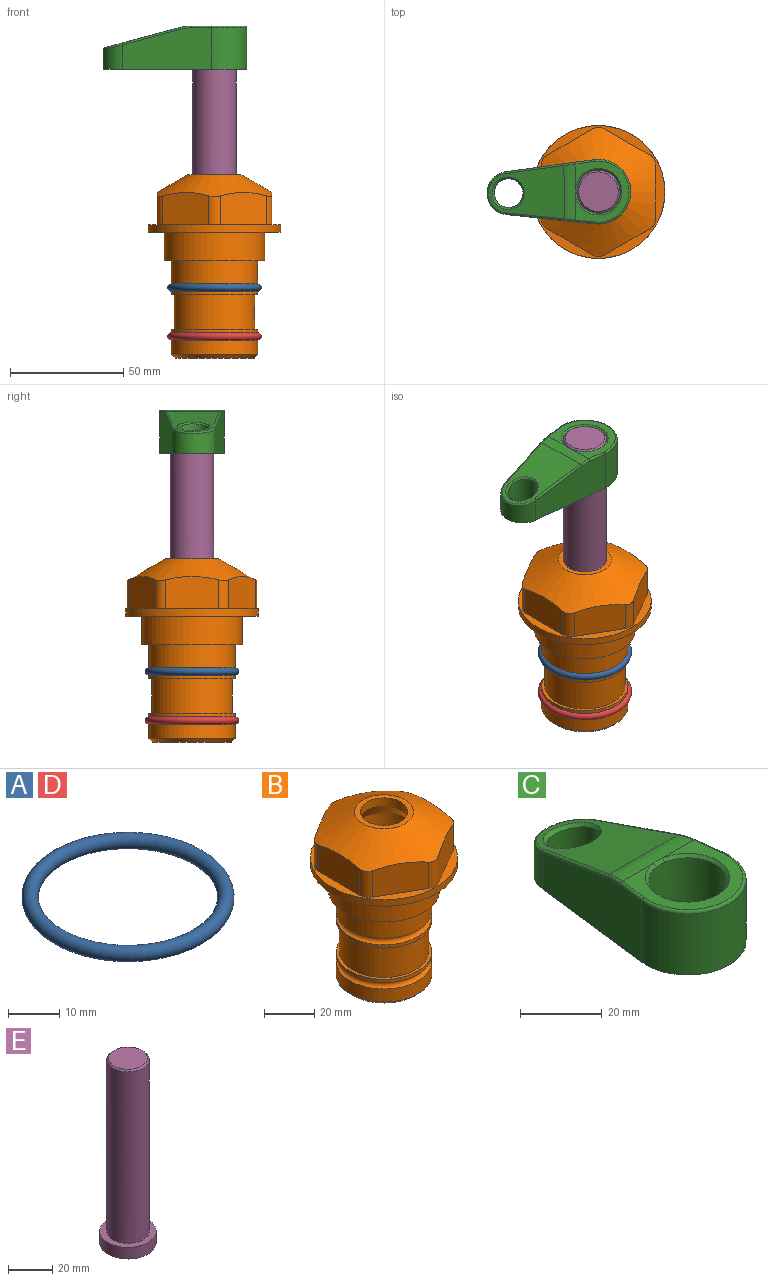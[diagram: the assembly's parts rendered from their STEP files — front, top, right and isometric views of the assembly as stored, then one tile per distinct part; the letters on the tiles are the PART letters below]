
ASSEMBLY  parts=5 mates=3
PART A: 1 faces, bbox 44.7x44.7x3.2 mm
  f0: torus R=19.05mm, axis (0,0,1), area 1193.9mm2
PART B: 36 faces, bbox 58.7x58.7x81 mm
  f0: cylinder r=17.78mm len=35.56mm, axis (0,0,1), area 1670.8mm2, adj f23,f24,f31
  f1: cylinder r=19.05mm len=38.1mm, axis (0,0,1), area 1191.9mm2, adj f26,f27,f30
  f2: plane 58.66x58.66mm, normal (0,0,-1), area 1150.6mm2, adj f3,f28
  f3: cylinder r=29.33mm len=58.66mm, axis (0,0,-1), area 585.1mm2, adj f2,f4
  f4: plane 58.66x58.66mm, normal (0,0,1), area 475.9mm2, adj f3,f5,f6,f7,f8,f9,f10,f11
  f5: plane 20.32x14.34mm, normal (-0.5,0.87,0), area 324.4mm2, adj f4,f15,f16,f17
  f6: plane 20.32x14.34mm, normal (0.5,0.87,0), area 324.4mm2, adj f4,f14,f15,f17
  f7: plane 23.48x14.34mm, normal (1,0,0), area 324.4mm2, adj f4,f13,f14,f17
  f8: plane 20.32x14.34mm, normal (0.5,-0.87,0), area 324.4mm2, adj f4,f12,f13,f17
  f9: plane 20.32x14.34mm, normal (-0.5,-0.87,0), area 324.4mm2, adj f4,f11,f12,f17
  f10: plane 23.48x14.34mm, normal (-1,0,0), area 324.4mm2, adj f4,f11,f16,f17
  f11: cylinder r=5.08mm len=12.85mm, axis (0,0,-1), area 67.2mm2, adj f4,f9,f10,f17
  f12: cylinder r=5.08mm len=12.85mm, axis (0,0,-1), area 67.2mm2, adj f4,f8,f9,f17
  f13: cylinder r=5.08mm len=12.85mm, axis (0,0,-1), area 67.2mm2, adj f4,f7,f8,f17
  f14: cylinder r=5.08mm len=12.85mm, axis (0,0,-1), area 67.2mm2, adj f4,f6,f7,f17
  f15: cylinder r=5.08mm len=12.85mm, axis (0,0,-1), area 67.2mm2, adj f4,f5,f6,f17
  f16: cylinder r=5.08mm len=12.85mm, axis (0,0,-1), area 67.2mm2, adj f4,f5,f10,f17
  f17: cone r=11.73mm half-angle=60deg, axis (0,0,-1), area 2071.8mm2, adj f5,f6,f7,f8,f9,f10,f11,f12
  f18: plane 23.46x23.46mm, normal (0,0,1), area 147.4mm2, adj f17,f35
  f19: plane 34.93x34.93mm, normal (0,0,-1), area 958mm2, adj f29
  f20: cylinder r=19.05mm len=38.1mm, axis (0,0,1), area 760.1mm2, adj f21,f29
  f21: torus R=19.05mm, axis (0,0,1), area 565.3mm2, adj f20,f22
  f22: cylinder r=19.05mm len=38.1mm, axis (0,0,1), area 190mm2, adj f21,f23
  f23: plane 38.1x38.1mm, normal (0,0,1), area 146.9mm2, adj f0,f22
  f24: plane 38.1x38.1mm, normal (0,0,-1), area 146.9mm2, adj f0,f25
  f25: cylinder r=19.05mm len=38.1mm, axis (0,0,1), area 190mm2, adj f24,f26
  f26: torus R=19.05mm, axis (0,0,1), area 565.3mm2, adj f1,f25
  f27: plane 44.45x44.45mm, normal (0,0,-1), area 411.7mm2, adj f1,f28
  f28: cylinder r=22.23mm len=44.45mm, axis (0,0,1), area 1773.5mm2, adj f2,f27
  f29: cone r=19.05mm half-angle=45deg, axis (0,0,1), area 257.5mm2, adj f19,f20
  f30: cylinder r=3.17mm len=6.75mm, axis (-1,0,0), area 128mm2, adj f1,f33
  f31: cylinder r=3.17mm len=6.35mm, axis (-1,0,0), area 102.5mm2, adj f0,f33
  f32: plane 25.4x25.4mm, normal (0,0,1), area 506.7mm2, adj f33
  f33: cylinder r=12.7mm len=66.42mm, axis (0,0,-1), area 5236.2mm2, adj f30,f31,f32,f34
  f34: cone r=9.53mm half-angle=30deg, axis (0,0,-1), area 443.4mm2, adj f33,f35
  f35: cylinder r=9.53mm len=19.05mm, axis (0,0,-1), area 240.9mm2, adj f18,f34
PART C: 31 faces, bbox 31.7x65.5x19.8 mm
  f0: plane 39.12x18.26mm, normal (0.99,0.12,0), area 612.2mm2, adj f1,f4,f7,f11,f13,f15
  f1: cylinder r=9.53mm len=18.91mm, axis (0,0,-1), area 296.1mm2, adj f0,f2,f7,f17
  f2: plane 39.12x18.26mm, normal (-0.99,0.12,0), area 612.2mm2, adj f1,f4,f7,f12,f14,f16
  f3: cylinder r=6.35mm len=12.7mm, axis (0,0,-1), area 362.4mm2, adj f7,f18
  f4: cylinder r=14.29mm len=28.58mm, axis (0,0,-1), area 882.2mm2, adj f0,f2,f7,f10
  f5: cylinder r=9.53mm len=19.05mm, axis (0,0,-1), area 1092.6mm2, adj f7,f19,f20
  f6: plane 26.99x23.69mm, normal (0,0,1), area 216.2mm2, adj f9,f10,f11,f12,f19
  f7: plane 63.5x28.58mm, normal (0,0,-1), area 661.8mm2, adj f0,f1,f2,f3,f4,f5,f22,f23
  f8: plane 33.52x23.6mm, normal (0,0.26,0.97), area 486mm2, adj f9,f15,f16,f17,f18
  f9: cylinder r=19.05mm len=24.72mm, axis (1,0,0), area 120.4mm2, adj f6,f8,f13,f14,f20
  f10: torus R=13.49mm, axis (0,0,1), area 59mm2, adj f4,f6,f11,f12
  f11: cylinder r=0.79mm len=8.67mm, axis (0.12,-0.99,0), area 10.8mm2, adj f0,f6,f10,f13
  f12: cylinder r=0.79mm len=8.67mm, axis (0.12,0.99,0), area 10.8mm2, adj f2,f6,f10,f14
  f13: bspline ~4.95x1.42mm, area 6.1mm2, adj f0,f9,f11,f15
  f14: bspline ~4.95x1.42mm, area 6.1mm2, adj f2,f9,f12,f16
  f15: cylinder r=0.79mm len=25.95mm, axis (0.12,-0.96,0.26), area 32.9mm2, adj f0,f8,f13,f17
  f16: cylinder r=0.79mm len=25.95mm, axis (0.12,0.96,-0.26), area 32.9mm2, adj f2,f8,f14,f17
  f17: bspline ~18.91x8.38mm, area 30mm2, adj f1,f8,f15,f16
  f18: bspline ~14.29x14.29mm, area 48.3mm2, adj f3,f8
  f19: cone r=9.53mm half-angle=45deg, axis (0,0,1), area 66.5mm2, adj f5,f6,f20
  f20: bspline ~3.22x0.96mm, area 3.5mm2, adj f5,f9,f19
  f21: plane 2.75x2.72mm, normal (0,0,-1), area 2.9mm2, adj f23,f25,f28
  f22: plane 23.05x15.88mm, normal (-0.99,-0.12,0), area 323.6mm2, adj f7,f25,f26,f27,f28,f29
  f23: plane 23.05x15.88mm, normal (0.99,-0.12,0), area 323.6mm2, adj f7,f21,f25,f27,f28,f30
  f24: cylinder r=9.53mm len=10.69mm, axis (0,0,-1), area 114.7mm2, adj f7,f27,f29,f30
  f25: cylinder r=12.7mm len=20.59mm, axis (0,0,-1), area 381.1mm2, adj f7,f21,f22,f23,f26,f28
  f26: plane 2.75x2.72mm, normal (0,0,-1), area 2.9mm2, adj f22,f25,f28
  f27: plane 19.72x18.37mm, normal (0,-0.26,-0.97), area 291.8mm2, adj f22,f23,f24,f28,f29,f30
  f28: cylinder r=15.88mm len=19.92mm, axis (1,0,0), area 54.8mm2, adj f21,f22,f23,f25,f26,f27
  f29: cylinder r=1.59mm len=11mm, axis (0,0,-1), area 34.7mm2, adj f7,f22,f24,f27
  f30: cylinder r=1.59mm len=11mm, axis (0,0,-1), area 34.7mm2, adj f7,f23,f24,f27
PART D: same geometry as A
PART E: 6 faces, bbox 25.4x25.4x101.6 mm
  f0: plane 17.46x17.46mm, normal (0,0,1), area 239.5mm2, adj f5
  f1: plane 25.4x25.4mm, normal (0,0,-1), area 506.7mm2, adj f2
  f2: cylinder r=12.7mm len=25.4mm, axis (0,0,1), area 506.7mm2, adj f1,f3
  f3: plane 25.4x25.4mm, normal (0,0,1), area 221.7mm2, adj f2,f4
  f4: cylinder r=9.53mm len=94.46mm, axis (0,0,1), area 5653mm2, adj f3,f5
  f5: cone r=8.73mm half-angle=45deg, axis (0,0,-1), area 64.4mm2, adj f0,f4
PLACE A at identity
PLACE B at identity fixed
PLACE C rot(axis=(0,0,1),90.9deg) t=(0,0,27.55)mm
PLACE D t=(0,0,-21.59)mm
PLACE E rot(axis=(0,0,1),90.9deg) t=(0,0,27.55)mm
MATE fastened D.f0 <-> B.f0  axis (0,0,1) through (0,0,-46.1)mm
MATE cylindrical E.f2 <-> B.f0  axis (0,0,-1) through (0,0,-10.55)mm
MATE fastened C.f4 <-> E.f2  axis (0,0,1) through (0,0,91.05)mm
